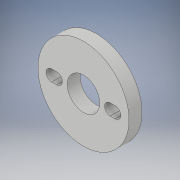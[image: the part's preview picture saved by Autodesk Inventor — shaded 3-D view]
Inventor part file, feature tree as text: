
AUTODESK INVENTOR PART (.ipt)
format: ipt  version: 2019 (Build 230136000, 136)  size: 122,880 bytes
history: native  units: mm
features: extrude x2, sketch x2
ambient origin geometry x8: Origin, YZ Plane, XZ Plane, XY Plane, X Axis, Y Axis, Z Axis, Center Point
bodies: Solid1 (feature_tree)
feature tree (4):
  extrude  "Extrusion1"  Depth=4.0mm TaperAngle=0.0deg
  extrude  "Extrusion2"  Depth=5.0mm
  sketch  "Sketch1"  dims[d0=28.0mm d1=4.0mm d2=0.0mm]
  sketch  "Sketch2"  dims[d3=10.0mm d4=5.0mm d5=3.5mm d6=6.5mm d7=5.0mm d8=5.0mm d9=0.0mm d11=6.5mm d12=1.5mm]
